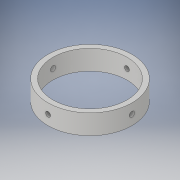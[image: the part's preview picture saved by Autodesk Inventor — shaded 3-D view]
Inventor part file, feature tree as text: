
AUTODESK INVENTOR PART (.ipt)
format: ipt  version: 2017 SP1 (Build 210196100, 196)  size: 124,416 bytes
history: native  units: in
note: dims shown in document units (in); Inventor stores cm internally (conversion verified against a paired STEP export)
features: sketch x3, plane x2, hole x2, extrude x1
ambient origin geometry x8: Origin, YZ Plane, XZ Plane, XY Plane, X Axis, Y Axis, Z Axis, Center Point
bodies: Solid1 (feature_tree)
feature tree (8):
  extrude  "Extrusion1"  Depth=4.25in
  plane  "Work Plane1"
  hole  "Hole1"  [1 undecoded]
  plane  "Work Plane2"
  hole  "Hole2"  [1 undecoded]
  sketch  "Sketch1"  dims[d0=3.75in d1=4.25in]
  sketch  "Sketch2"  dims[d2=1.0in d3=0.0in]
  sketch  "Sketch3"  dims[d4=2.125in d5=0.25in d6=0.75in d7=0.375in d8=0.25in d9=0.5635in d10=1.0in d11=0.8108in d12=2.125in d13=0.266in d14=0.75in d15=0.507in d16=0.25in d17=0.5635in d18=1.0in d19=0.8108in]
note: 2 required parameter values undecoded (feature->parameter linkage not recoverable at this tier; creation-order binding heuristic only, values carry confidence <= 0.55)
